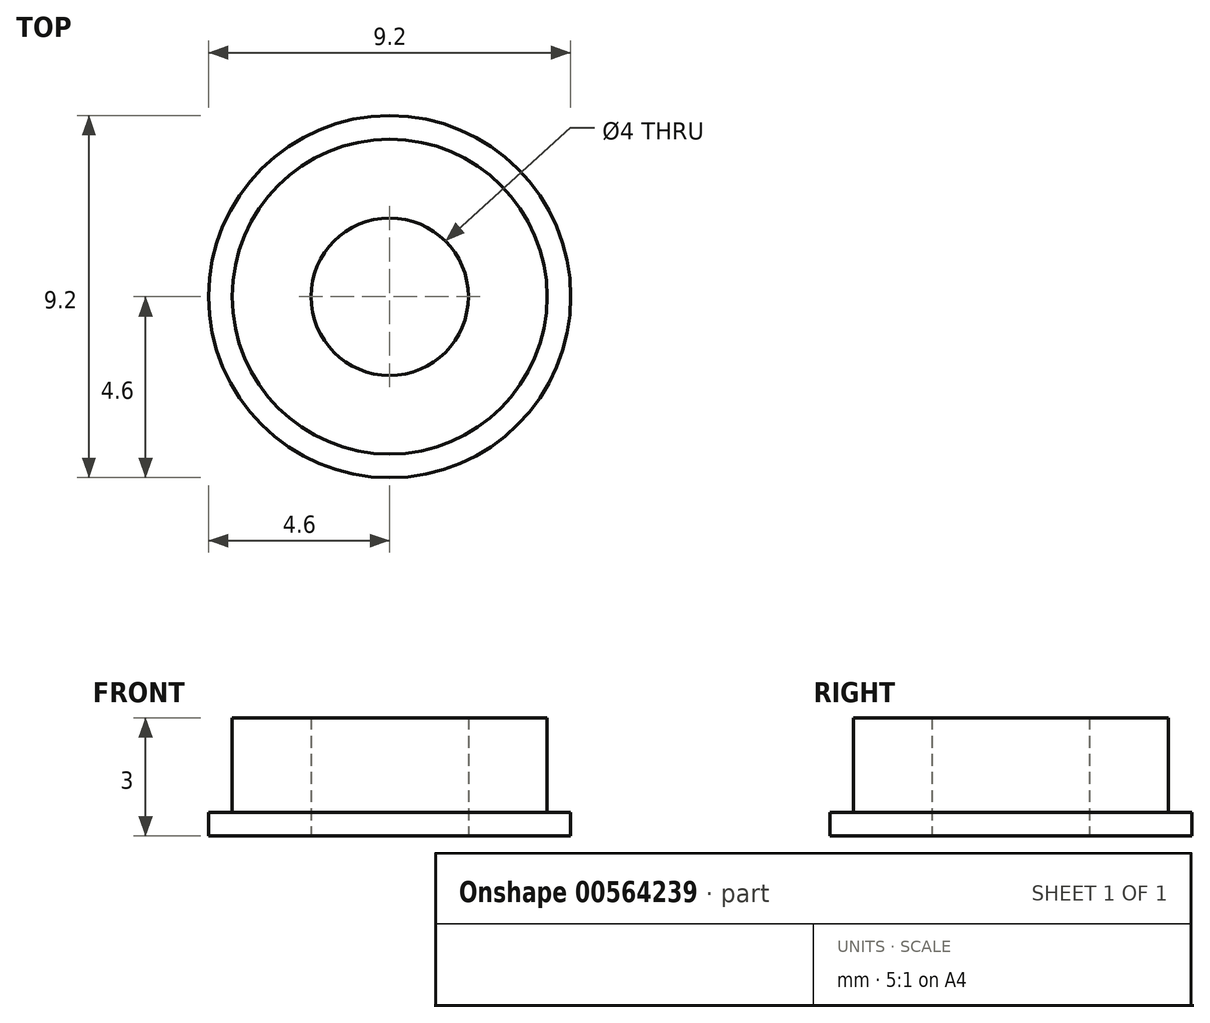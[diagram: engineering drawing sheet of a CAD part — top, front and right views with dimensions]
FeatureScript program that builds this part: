
annotation { "Feature Type Name" : "Feature", "Feature Type Description" : "" }
export const myFeature = defineFeature(function(context is Context, id is Id, definition is map)
    precondition{}
    {
        {
            var Q0;
            Q0=qCreatedBy(makeId("Top.planeOp"),FACE);
            var sketch = newSketch(context, id + "F0", { "sketchPlane" : qUnion([Q0])});
            skCircle(sketch, "E0", {"center": v(0, 0) * mm, "radius": 2 * mm});
            skCircle(sketch, "E1", {"center": v(0, 0) * mm, "radius": 4 * mm});
            skCircle(sketch, "E2", {"center": v(0, 0) * mm, "radius": 4.6 * mm});
            skSolve(sketch);
        }
        {
            var Q0;
            Q0=makeQuery(id+"F0.imprint","IMPRINT",FACE,{"disambiguationData":[TD([[makeQuery(id+"F0.imprint","IMPRINT",EDGE,{"derivedFrom":sQuery(id+"F0.wireOp",EDGE,"E0")}),-1.0]])]});
            extrude(context, id + "F1", {"entities" : qUnion([Q0]), "depth" : 3 * mm, "offsetDistance" : 25 * mm});
        }
        {
            assignVariable(context, id + "F2", {"name" : "FlangeWidth", "anyValue" : 0.6 * mm});
        }
        {
            var Q0;
            Q0=makeQuery(id+"F0.imprint","IMPRINT",FACE,{"disambiguationData":[TD([[makeQuery(id+"F0.imprint","IMPRINT",EDGE,{"derivedFrom":sQuery(id+"F0.wireOp",EDGE,"E1")}),-1.0]])]});
            extrude(context, id + "F3", {"entities" : qUnion([Q0]), "operationType" : NewBodyOperationType.ADD, "depth" : getVariable(context, 'FlangeWidth'), "offsetDistance" : 25 * mm});
        }
    });
